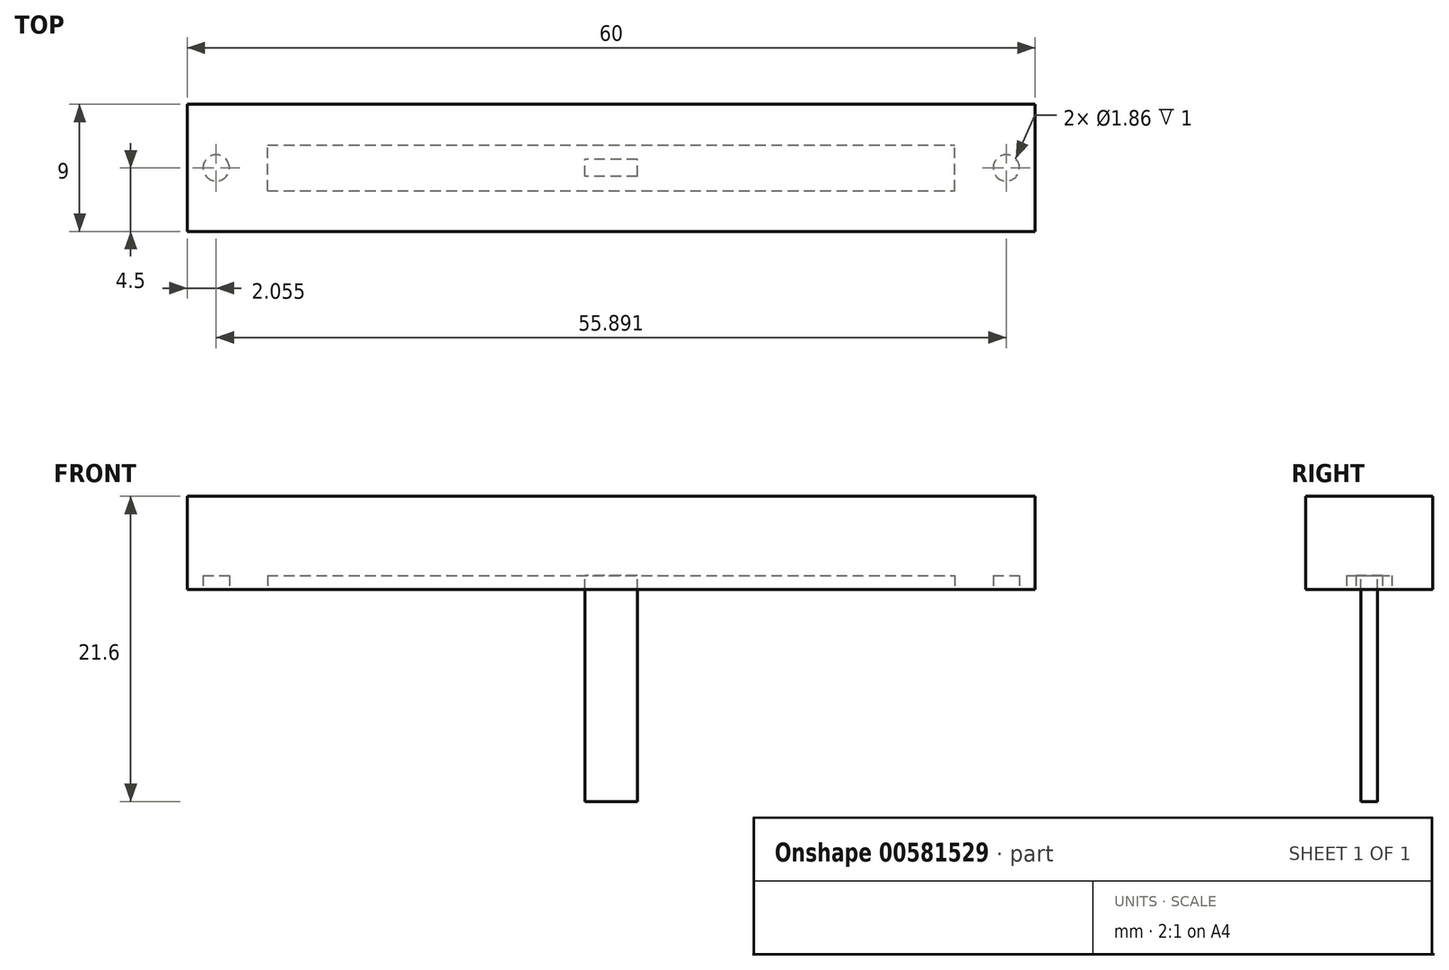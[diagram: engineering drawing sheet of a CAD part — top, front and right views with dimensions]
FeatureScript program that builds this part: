
annotation { "Feature Type Name" : "Feature", "Feature Type Description" : "" }
export const myFeature = defineFeature(function(context is Context, id is Id, definition is map)
    precondition{}
    {
        {
            var Q0;
            Q0=qCreatedBy(makeId("Top.planeOp"),FACE);
            var sketch = newSketch(context, id + "F0", { "sketchPlane" : qUnion([Q0])});
            skLineSegment(sketch, "E0.bottom", {"start": v(-30, 4.5) * mm, "end": v(30, 4.5) * mm});
            skLineSegment(sketch, "E0.top", {"start": v(-30, -4.5) * mm, "end": v(30, -4.5) * mm});
            skLineSegment(sketch, "E0.left", {"start": v(-30, 4.5) * mm, "end": v(-30, -4.5) * mm});
            skLineSegment(sketch, "E0.right", {"start": v(30, 4.5) * mm, "end": v(30, -4.5) * mm});
            skPoint(sketch, "E0.middle", {"position": v(0, 0) * mm});
            skSolve(sketch);
        }
        {
            var Q0;
            Q0 = qSketchRegion(id + "F0", true);
            extrude(context, id + "F1", {"entities" : qUnion([Q0]), "oppositeDirection" : true, "depth" : 6.6 * mm, "offsetDistance" : 25 * mm});
        }
        {
            var Q0;
            Q0=makeQuery(id+"F1.opExtrude","CAP_FACE",FACE,{"disambiguationData":[OSD([sQuery(id+"F0.wireOp",EDGE,"E0.bottom"),sQuery(id+"F0.wireOp",EDGE,"E0.top"),sQuery(id+"F0.wireOp",EDGE,"E0.left"),sQuery(id+"F0.wireOp",EDGE,"E0.right")])],"isStart":false});
            var sketch = newSketch(context, id + "F2", { "sketchPlane" : qUnion([Q0])});
            skLineSegment(sketch, "E1.bottom", {"start": v(-24.31, 1.6) * mm, "end": v(24.31, 1.6) * mm});
            skLineSegment(sketch, "E1.top", {"start": v(-24.31, -1.6) * mm, "end": v(24.31, -1.6) * mm});
            skLineSegment(sketch, "E1.left", {"start": v(-24.31, 1.6) * mm, "end": v(-24.31, -1.6) * mm});
            skLineSegment(sketch, "E1.right", {"start": v(24.31, 1.6) * mm, "end": v(24.31, -1.6) * mm});
            skPoint(sketch, "E1.middle", {"position": v(0, 0) * mm});
            skCircle(sketch, "E2", {"center": v(-27.95, 0) * mm, "radius": 0.93 * mm});
            skCircle(sketch, "E3.MirrorC", {"center": v(27.95, 0) * mm, "radius": 0.93 * mm});
            skSolve(sketch);
        }
        {
            var Q0;
            Q0 = qSketchRegion(id + "F2", true);
            extrude(context, id + "F3", {"entities" : qUnion([Q0]), "operationType" : NewBodyOperationType.REMOVE, "oppositeDirection" : true, "depth" : 1 * mm, "offsetDistance" : 25 * mm});
        }
        {
            var Q0;
            Q0=makeQuery(id+"F1.opExtrude","CAP_FACE",FACE,{"disambiguationData":[OSD([sQuery(id+"F0.wireOp",EDGE,"E0.bottom"),sQuery(id+"F0.wireOp",EDGE,"E0.top"),sQuery(id+"F0.wireOp",EDGE,"E0.left"),sQuery(id+"F0.wireOp",EDGE,"E0.right")])],"isStart":true});
            var sketch = newSketch(context, id + "F4", { "sketchPlane" : qUnion([Q0])});
            skLineSegment(sketch, "E4.bottom", {"start": v(-1.85, 0.6) * mm, "end": v(1.85, 0.6) * mm});
            skLineSegment(sketch, "E4.top", {"start": v(-1.85, -0.6) * mm, "end": v(1.85, -0.6) * mm});
            skLineSegment(sketch, "E4.left", {"start": v(-1.85, 0.6) * mm, "end": v(-1.85, -0.6) * mm});
            skLineSegment(sketch, "E4.right", {"start": v(1.85, 0.6) * mm, "end": v(1.85, -0.6) * mm});
            skPoint(sketch, "E4.middle", {"position": v(0, 0) * mm});
            skSolve(sketch);
        }
        {
            var Q0;
            Q0 = qSketchRegion(id + "F4", true);
            extrude(context, id + "F5", {"entities" : qUnion([Q0]), "operationType" : NewBodyOperationType.ADD, "oppositeDirection" : true, "depth" : 21.6 * mm, "offsetDistance" : 25 * mm});
        }
    });
